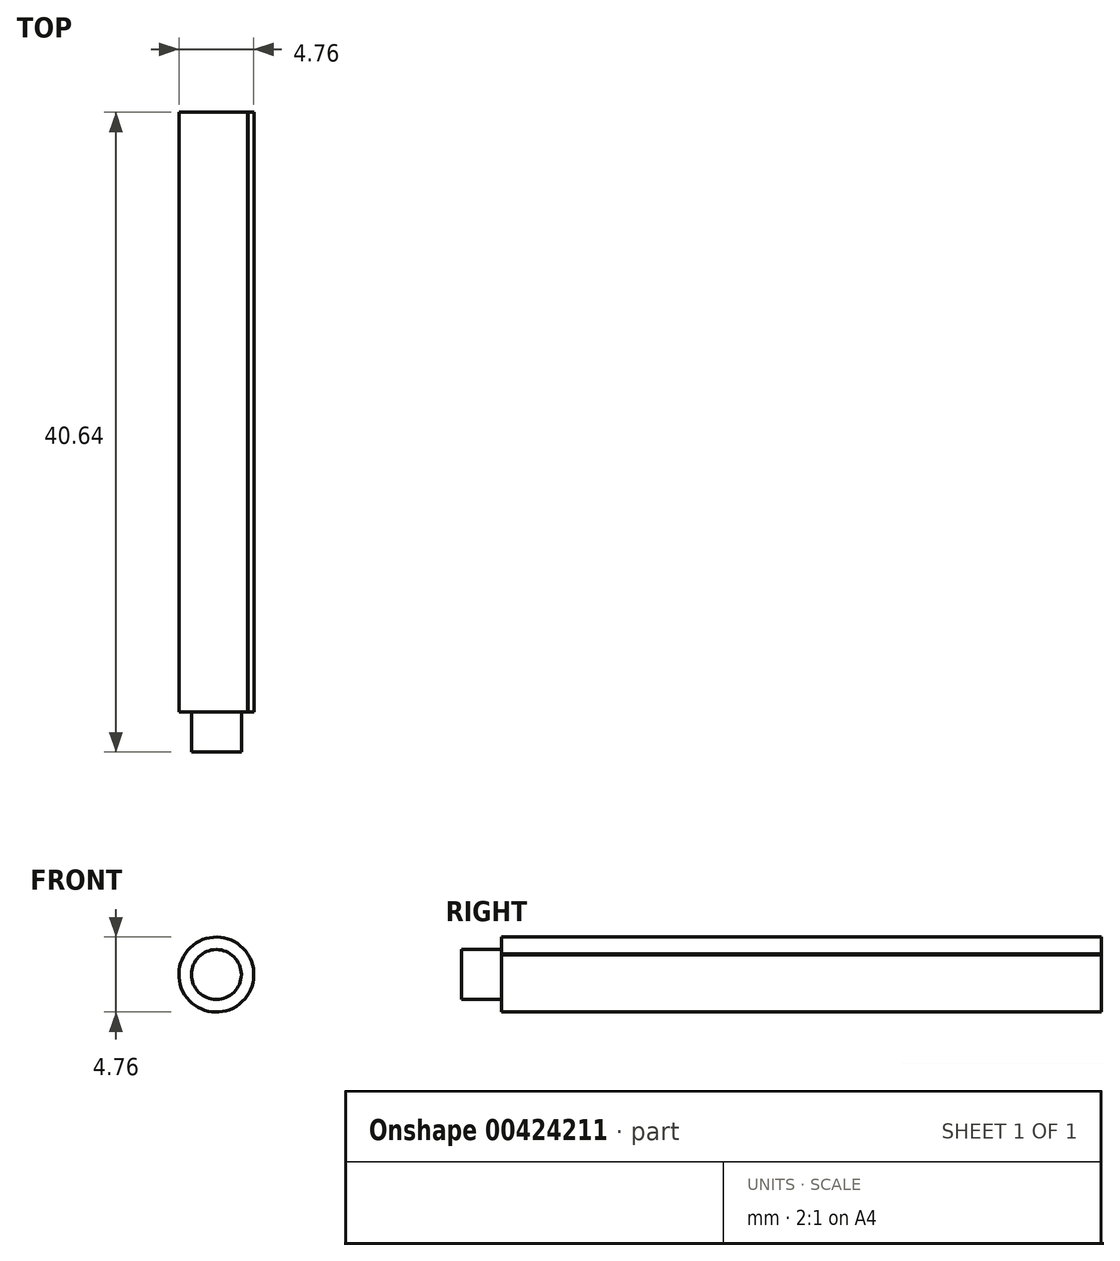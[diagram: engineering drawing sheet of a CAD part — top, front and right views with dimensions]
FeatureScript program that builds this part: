
annotation { "Feature Type Name" : "Feature", "Feature Type Description" : "" }
export const myFeature = defineFeature(function(context is Context, id is Id, definition is map)
    precondition{}
    {
        {
            var Q0;
            Q0=qCreatedBy(makeId("Front.planeOp"),FACE);
            var sketch = newSketch(context, id + "F0", { "sketchPlane" : qUnion([Q0])});
            skCircle(sketch, "E0", {"center": v(0, 0) * mm, "radius": 2.38 * mm});
            skCircle(sketch, "E1", {"center": v(0, 0) * mm, "radius": 1.59 * mm});
            skFitSpline(sketch, "E2", {"points": [v(0, 2.38) * mm, v(-16.54, 21.66) * mm], "startDerivative": vector(-8.5, 10.53) * mm, "endDerivative": vector(-32.58, -1.1) * mm});
            skFitSpline(sketch, "E3", {"points": [v(-16.54, 21.66) * mm, v(-1.95, -1.37) * mm], "startDerivative": vector(-19.65, -78.49) * mm, "endDerivative": vector(14.59, -23.03) * mm});
            skFitSpline(sketch, "E4", {"points": [v(-0.08, -2.38) * mm, v(15.88, -22.14) * mm], "startDerivative": vector(8.5, -10.53) * mm, "endDerivative": vector(32.58, 1.1) * mm});
            skFitSpline(sketch, "E5", {"points": [v(15.88, -22.14) * mm, v(2, 1.3) * mm], "startDerivative": vector(19.65, 78.49) * mm, "endDerivative": vector(-14.59, 23.03) * mm});
            skSolve(sketch);
        }
        {
            var Q0;
            {var subQ0=sQuery(id+"F0.wireOp",EDGE,"E3");var subQ1=sQuery(id+"F0.wireOp",EDGE,"E0");var subQ2=makeQuery(id+"F0.imprint","INTERSECT",VERTEX,{"disambiguationData":[OD(0.0)],"derivedFrom":[subQ1,subQ0]});Q0=makeQuery(id+"F0.imprint","IMPRINT",FACE,{"disambiguationData":[TD([[makeQuery(id+"F0.imprint","IMPRINT",EDGE,{"disambiguationData":[TD([[subQ2,1.0]])],"derivedFrom":subQ1}),1.0]])]});}
            var Q1;
            Q1=makeQuery(id+"F0.imprint","IMPRINT",FACE,{"disambiguationData":[TD([[makeQuery(id+"F0.imprint","IMPRINT",EDGE,{"derivedFrom":sQuery(id+"F0.wireOp",EDGE,"E1")}),-1.0]])]});
            extrude(context, id + "F1", {"entities" : qUnion([Q0, Q1]), "depth" : 38.1 * mm});
        }
        {
            var Q0;
            Q0=makeQuery(id+"F0.imprint","IMPRINT",FACE,{"disambiguationData":[TD([[makeQuery(id+"F0.imprint","IMPRINT",EDGE,{"derivedFrom":sQuery(id+"F0.wireOp",EDGE,"E1")}),1.0]])]});
            var Q1;
            Q1=sQuery(id+"F0.wireOp",EDGE,"E1");
            extrude(context, id + "F2", {"entities" : qUnion([Q0]), "operationType" : NewBodyOperationType.ADD, "surfaceEntities" : qUnion([Q1]), "depth" : 40.64 * mm});
        }
    });
